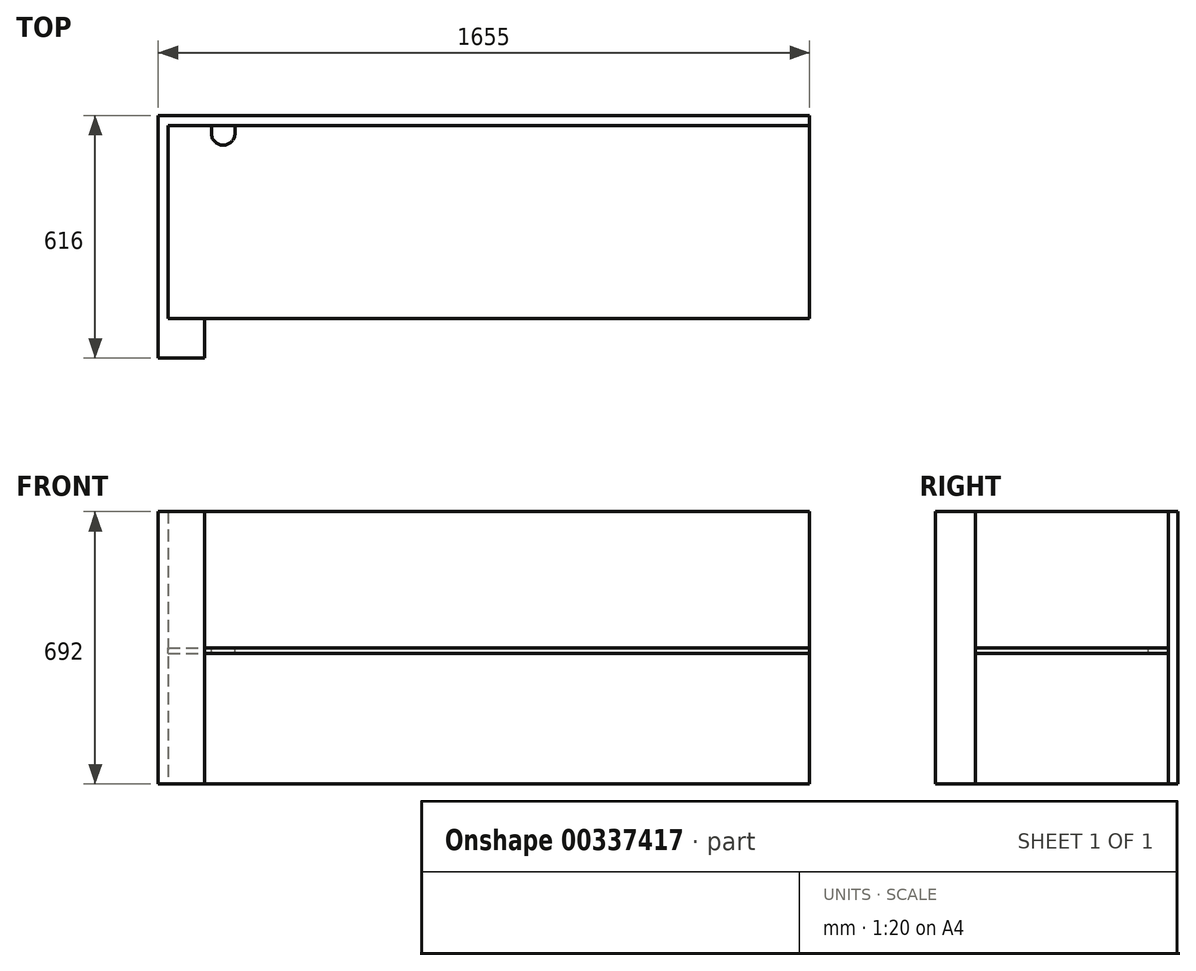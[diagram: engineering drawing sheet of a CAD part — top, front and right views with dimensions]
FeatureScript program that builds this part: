
annotation { "Feature Type Name" : "Feature", "Feature Type Description" : "" }
export const myFeature = defineFeature(function(context is Context, id is Id, definition is map)
    precondition{}
    {
        {
            var Q0;
            Q0=qCreatedBy(makeId("Top.planeOp"),FACE);
            var sketch = newSketch(context, id + "F0", { "sketchPlane" : qUnion([Q0])});
            skLineSegment(sketch, "E0.bottom", {"start": v(-815, 245) * mm, "end": v(-705, 245) * mm});
            skLineSegment(sketch, "E0.top", {"start": v(-815, -245) * mm, "end": v(815, -245) * mm});
            skLineSegment(sketch, "E0.left", {"start": v(-815, 245) * mm, "end": v(-815, -245) * mm});
            skLineSegment(sketch, "E0.right", {"start": v(815, 245) * mm, "end": v(815, -245) * mm});
            skLineSegment(sketch, "E1", {"start": v(-645, 245) * mm, "end": v(815, 245) * mm});
            skLineSegment(sketch, "E2", {"start": v(-705, 245) * mm, "end": v(-705, 225) * mm});
            skLineSegment(sketch, "E3", {"start": v(-645, 245) * mm, "end": v(-645, 225) * mm});
            skArc(sketch, "E4", {"start": v(-705, 225) * mm, "mid": v(-675, 195) * mm, "end": v(-645, 225) * mm});
            skLineSegment(sketch, "E5", {"start": v(-815, -245) * mm, "end": v(815, 245) * mm, "construction": true});
            skSolve(sketch);
        }
        {
            var Q0;
            Q0=makeQuery(id+"F0.imprint","IMPRINT",FACE,{"disambiguationData":[TD([[makeQuery(id+"F0.imprint","IMPRINT",EDGE,{"derivedFrom":sQuery(id+"F0.wireOp",EDGE,"E0.bottom")}),-1.0]])]});
            extrude(context, id + "F1", {"entities" : qUnion([Q0]), "oppositeDirection" : true, "depth" : 15 * mm});
        }
        {
            var Q0;
            Q0=makeQuery(id+"F1.opExtrude","CAP_FACE",FACE,{"disambiguationData":[OSD([sQuery(id+"F0.wireOp",EDGE,"E0.bottom"),sQuery(id+"F0.wireOp",EDGE,"E0.top"),sQuery(id+"F0.wireOp",EDGE,"E0.left"),sQuery(id+"F0.wireOp",EDGE,"E0.right"),sQuery(id+"F0.wireOp",EDGE,"E1"),sQuery(id+"F0.wireOp",EDGE,"E2"),sQuery(id+"F0.wireOp",EDGE,"E3"),sQuery(id+"F0.wireOp",EDGE,"E4")])],"isStart":true});
            var sketch = newSketch(context, id + "F2", { "sketchPlane" : qUnion([Q0])});
            skLineSegment(sketch, "E6", {"start": v(-815, -245) * mm, "end": v(-815, 245) * mm});
            skLineSegment(sketch, "E7", {"start": v(-815, 245) * mm, "end": v(815, 245) * mm});
            skLineSegment(sketch, "E8", {"start": v(815, 245) * mm, "end": v(815, 270) * mm});
            skLineSegment(sketch, "E9", {"start": v(815, 270) * mm, "end": v(-840, 270) * mm});
            skLineSegment(sketch, "E10", {"start": v(-840, 270) * mm, "end": v(-840, -346) * mm});
            skLineSegment(sketch, "E11", {"start": v(-840, -346) * mm, "end": v(-722, -346) * mm});
            skLineSegment(sketch, "E12", {"start": v(-722, -346) * mm, "end": v(-722, -245) * mm});
            skLineSegment(sketch, "E13", {"start": v(-722, -245) * mm, "end": v(-815, -245) * mm});
            skSolve(sketch);
        }
        {
            var Q0;
            {var subQ4=sQuery(id+"F2.wireOp",EDGE,"E6");Q0=makeQuery(id+"F2.imprint","IMPRINT",FACE,{"disambiguationData":[TD([[makeQuery(id+"F2.imprint","IMPRINT",EDGE,{"derivedFrom":subQ4}),-1.0]])]});}
            extrude(context, id + "F3", {"entities" : qUnion([Q0]), "endBound" : BoundingType.SYMMETRIC, "depth" : 2 * 346 * mm});
        }
        {
            var Q0;
            Q0=makeQuery(id+"F3.opExtrude","SWEPT_FACE",FACE,{"disambiguationData":[OSD([sQuery(id+"F2.wireOp",EDGE,"E7")])]});
            var sketch = newSketch(context, id + "F4", { "sketchPlane" : qUnion([Q0])});
            skLineSegment(sketch, "E14", {"start": v(-695, 346) * mm, "end": v(-695, -346) * mm, "construction": true});
            skLineSegment(sketch, "E15", {"start": v(-95, 346) * mm, "end": v(-95, -346) * mm, "construction": true});
            skLineSegment(sketch, "E16", {"start": v(-815, 331) * mm, "end": v(815, 331) * mm, "construction": true});
            skLineSegment(sketch, "E17", {"start": v(-815, 302.5) * mm, "end": v(815, 302.5) * mm, "construction": true});
            skLineSegment(sketch, "E18", {"start": v(-815, 252.5) * mm, "end": v(815, 252.5) * mm, "construction": true});
            skLineSegment(sketch, "E19", {"start": v(-815, 148.5) * mm, "end": v(815, 148.5) * mm, "construction": true});
            skCircle(sketch, "E20", {"center": v(-695, 302.5) * mm, "radius": 4.5 * mm});
            skCircle(sketch, "E21", {"center": v(-695, 148.5) * mm, "radius": 4.5 * mm});
            skCircle(sketch, "E22", {"center": v(-95, 302.5) * mm, "radius": 4.5 * mm});
            skCircle(sketch, "E23", {"center": v(-95, 148.5) * mm, "radius": 4.5 * mm});
            skLineSegment(sketch, "E24.bottom", {"start": v(-455, 235) * mm, "end": v(-185, 235) * mm, "construction": true});
            skLineSegment(sketch, "E24.top", {"start": v(-455, 25) * mm, "end": v(-185, 25) * mm, "construction": true});
            skLineSegment(sketch, "E24.left", {"start": v(-455, 235) * mm, "end": v(-455, 25) * mm, "construction": true});
            skLineSegment(sketch, "E24.right", {"start": v(-185, 235) * mm, "end": v(-185, 25) * mm, "construction": true});
            skLineSegment(sketch, "E25", {"start": v(-455, 25) * mm, "end": v(-185, 235) * mm, "construction": true});
            skPoint(sketch, "E26", {"position": v(-320, 130) * mm});
            skLineSegment(sketch, "E27", {"start": v(-15, 346) * mm, "end": v(-15, 0) * mm, "construction": true});
            skSolve(sketch);
        }
    });
